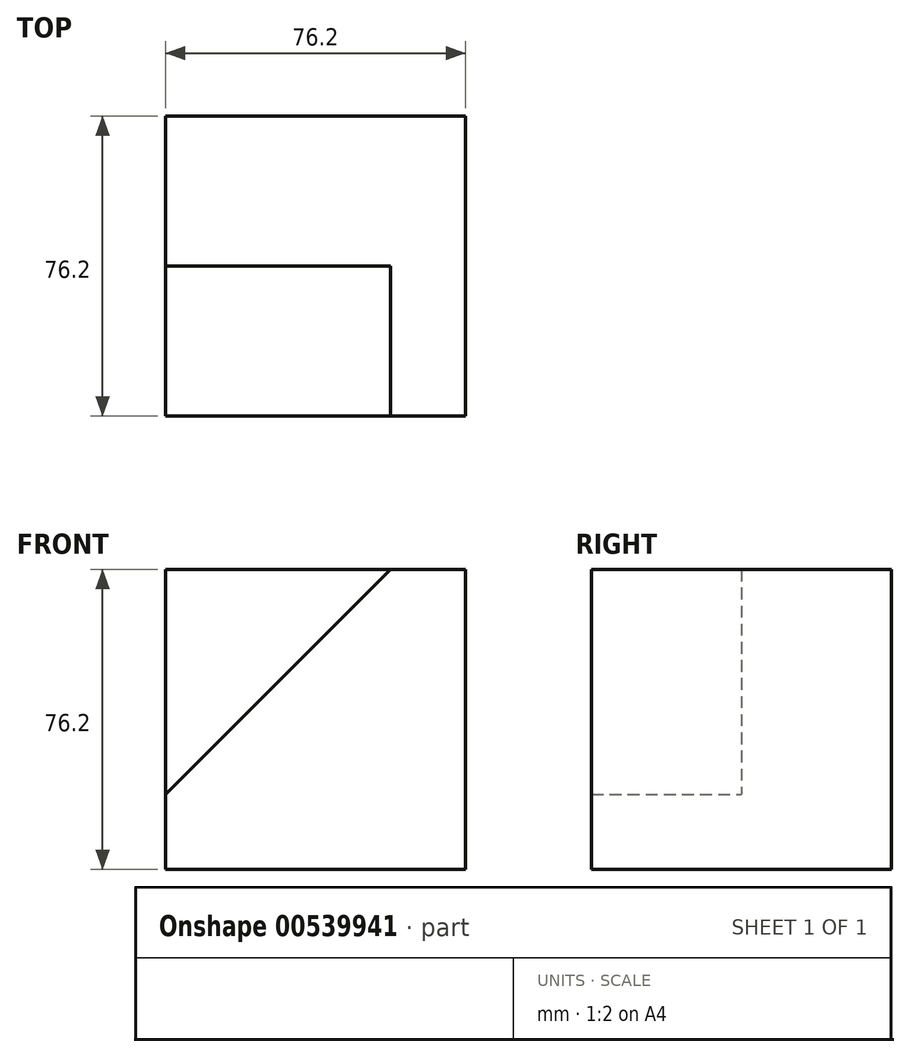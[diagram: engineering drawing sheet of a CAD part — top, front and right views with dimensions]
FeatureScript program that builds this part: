
annotation { "Feature Type Name" : "Feature", "Feature Type Description" : "" }
export const myFeature = defineFeature(function(context is Context, id is Id, definition is map)
    precondition{}
    {
        {
            var Q0;
            Q0=qCreatedBy(makeId("Front.planeOp"),FACE);
            var sketch = newSketch(context, id + "F0", { "sketchPlane" : qUnion([Q0])});
            skLineSegment(sketch, "E0", {"start": v(0, 0) * mm, "end": v(76.2, 0) * mm});
            skLineSegment(sketch, "E1", {"start": v(76.2, 0) * mm, "end": v(76.2, 76.2) * mm});
            skLineSegment(sketch, "E2", {"start": v(76.2, 76.2) * mm, "end": v(0, 76.2) * mm});
            skLineSegment(sketch, "E3", {"start": v(0, 76.2) * mm, "end": v(0, 0) * mm});
            skSolve(sketch);
        }
        {
            var Q0;
            Q0 = qSketchRegion(id + "F0", true);
            extrude(context, id + "F1", {"entities" : qUnion([Q0]), "depth" : 38.1 * mm, "offsetDistance" : 25.4 * mm});
        }
        {
            var Q0;
            Q0=makeQuery(id+"F1.opExtrude","CAP_FACE",FACE,{"disambiguationData":[OSD([sQuery(id+"F0.wireOp",EDGE,"E0"),sQuery(id+"F0.wireOp",EDGE,"E1"),sQuery(id+"F0.wireOp",EDGE,"E2"),sQuery(id+"F0.wireOp",EDGE,"E3")])],"isStart":false});
            var sketch = newSketch(context, id + "F2", { "sketchPlane" : qUnion([Q0])});
            skLineSegment(sketch, "E4", {"start": v(0, 0) * mm, "end": v(0, 19.05) * mm});
            skLineSegment(sketch, "E5", {"start": v(0, 19.05) * mm, "end": v(57.15, 76.2) * mm});
            skLineSegment(sketch, "E6", {"start": v(57.15, 76.2) * mm, "end": v(76.2, 76.2) * mm});
            skLineSegment(sketch, "E7", {"start": v(76.2, 76.2) * mm, "end": v(76.2, 0) * mm});
            skLineSegment(sketch, "E8", {"start": v(76.2, 0) * mm, "end": v(0, 0) * mm});
            skSolve(sketch);
        }
        {
            var Q0;
            Q0 = qSketchRegion(id + "F2", true);
            extrude(context, id + "F3", {"entities" : qUnion([Q0]), "operationType" : NewBodyOperationType.ADD, "depth" : 38.1 * mm, "offsetDistance" : 25.4 * mm});
        }
    });
